# Revit family: NLRS_63_LF_UN_noodverlichting HDN900_htk
name_source: partatom
category: Lighting Fixtures
units: mm (PartAtom-declared; Revit-internal decimal feet)

## family parameters
Always vertical = Yes
Cut with Voids When Loaded = No
Light Source = Yes
OmniClass Number = 23.85.30.21
OmniClass Title = Environmental Detection/Registration
Part Type = Normal
Room Calculation Point = No
Round Connector Dimension = Use Radius
Shared = No
Work Plane-Based = No

## types (3) — shared parameters
Apparent Load = 0 VA
Color Filter = 16777215
Dimming Lamp Color Temperature Shift = <None>
Emit from Line Length = 610 mm
Manufacturer = Hertek
NLRS_C_code_ETIM = EC001957
NLRS_C_code_ETIM_url = http://prod.etim-international.com
NLRS_C_code_fabrikant_gln = 8714253082646
NLRS_C_hoogte = 127 mm
NLRS_C_lengte = 222 mm  [stored 0.728346 ft]
NLRS_C_materiaal = <By Category>
NLRS_C_materiaal_01 = Glass
NLRS_C_omschrijving = LED 230v centraal
NLRS_E_IPwaarde = 22
NLRS_E_c01_radius = 8 mm  [stored 0.0262467 ft]
NLRS_E_c01_schijnbaar_vermogen = 0 VA
NLRS_E_c01_schijnbaar_vermogen_fase_1 = 0 VA
NLRS_E_c01_schijnbaar_vermogen_fase_2 = 0 VA
NLRS_E_c01_schijnbaar_vermogen_fase_3 = 0 VA
NLRS_E_spanning = 230 V
NLRS_E_stroom = 0.0 A
NLRS_S_gewicht_netto = 0.00 kg
Photometric Web File = EVOLUX_8W.ies
Tilt Angle = 90.00°
URL = www.hertek.eu
centraal = Yes
decentraal = No
vermogensclassificatie = NV

## per-type parameters (varying)
| type | NLRS_C_breedte | NLRS_C_code_artikel | NLRS_C_model | NLRS_C_offset_01 | NLRS_C_revit_versie | plafondmontage | reken04 | reken05 | reken06 | wandmontage | zichtbaar_01 | zichtbaar_02 |
| design centraal 230v_htk_HDC922A | 10 mm  [stored 0.0328084 ft] | HDC922A | design centraal 230v HDC922A | 11 mm  [stored 0.0360892 ft] | 2013 | No | 200 mm  [stored 0.656168 ft] | 275 mm | 15 mm  [stored 0.0492126 ft] | Yes | Yes | No |
| design centraal 230v_htk_HDC942A | 40 mm  [stored 0.131234 ft] | HDC942A | design centraal 230v HDC942A | 15 mm  [stored 0.0492126 ft] | 2014 | Yes | 0 mm  [stored 0 ft] | 120 mm  [stored 0.393701 ft] | 20 mm  [stored 0.0656168 ft] | No | No | No |
| design centraal 230v_htk_HDC992A | 40 mm  [stored 0.131234 ft] | HDC992A | design centraal 230v HDC992A | 15 mm  [stored 0.0492126 ft] | 2013 | Yes | 0 mm  [stored 0 ft] | 120 mm  [stored 0.393701 ft] | 20 mm  [stored 0.0656168 ft] | No | No | Yes |

note: [stored X ft] marks values corroborated as IEEE doubles in the binary element streams (Revit-internal decimal feet)

## geometry (parser evidence)
native form markers: Blend x6, Sweep x39
no freeform markers — native parametric forms only
